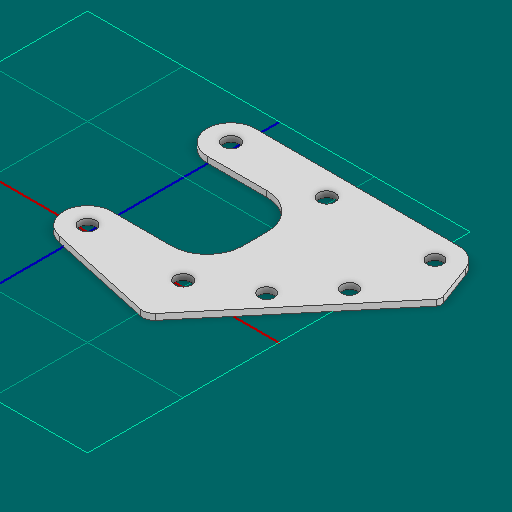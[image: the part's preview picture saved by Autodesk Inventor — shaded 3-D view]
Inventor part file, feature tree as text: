
AUTODESK INVENTOR PART (.ipt)
format: ipt  version: 2025 (Build 290162000, 162)  size: 149,504 bytes
history: native  units: in
note: dims shown in document units (in); Inventor stores cm internally (conversion verified against a paired STEP export)
features: other x6, sketch x1
ambient origin geometry x8: Origin, YZ Plane, XZ Plane, XY Plane, X Axis, Y Axis, Z Axis, Center Point
bodies: Solid1 (feature_tree)
feature tree (7):
  other  "funel_gusset_mirrored.ipt"
  other  "Blocks"
  other  "main"
  other  "Solid1::funel_gusset_mirrored.ipt"
  other  "TaggingFeature1"
  sketch  "Sketch1"  dims[d0=0.3937in d1=0.5in d6=0.375in d8=0.164in d9=0.0625in d14=0.164in d15=0.615in d17=0.125in]
  other  "main:1"
